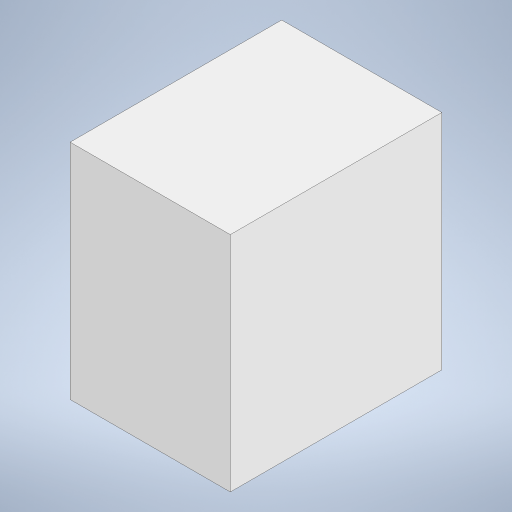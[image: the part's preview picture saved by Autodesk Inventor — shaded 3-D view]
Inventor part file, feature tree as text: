
AUTODESK INVENTOR PART (.ipt)
format: ipt  version: 2024 (Build 280153000, 153)  size: 166,400 bytes
history: native  units: in
note: dims shown in document units (in); Inventor stores cm internally (conversion verified against a paired STEP export)
features: extrude x1, sketch x1
ambient origin geometry x8: Origin, YZ Plane, XZ Plane, XY Plane, X Axis, Y Axis, Z Axis, Center Point
bodies: Solid1 (feature_tree)
feature tree (2):
  extrude  "Extrusion1"  Depth=30.375in
  sketch  "Sketch1"  dims[d1=32.0in d3=30.375in d4=23.0in d5=0.0in]
